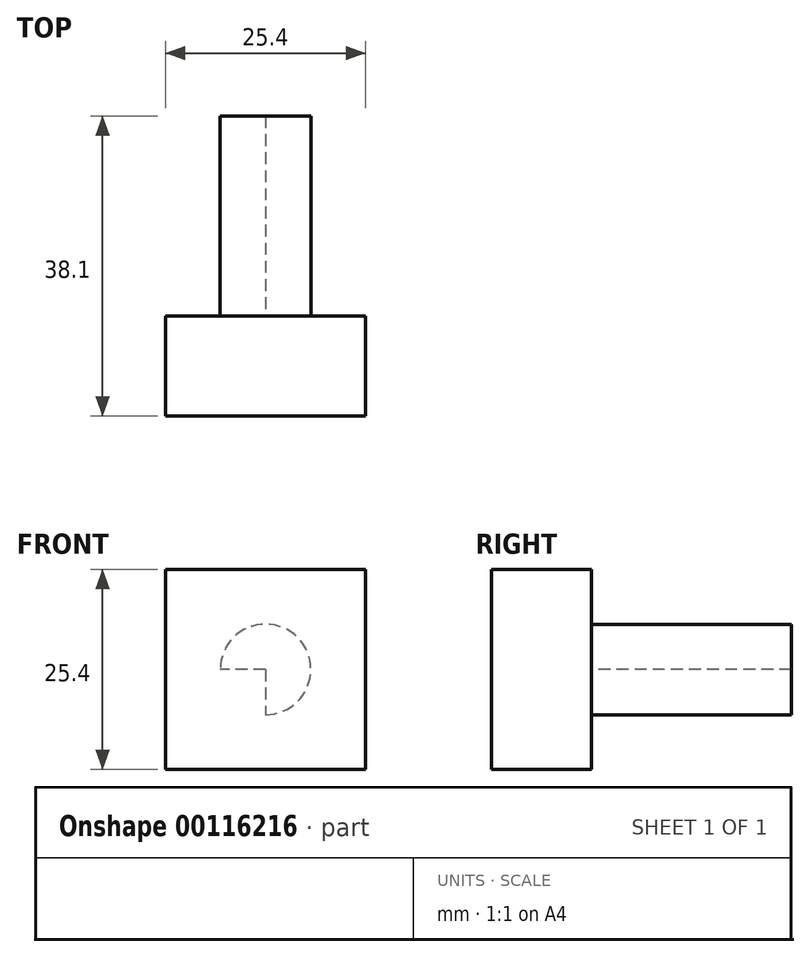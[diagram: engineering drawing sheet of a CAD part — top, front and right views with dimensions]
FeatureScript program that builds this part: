
annotation { "Feature Type Name" : "Feature", "Feature Type Description" : "" }
export const myFeature = defineFeature(function(context is Context, id is Id, definition is map)
    precondition{}
    {
        {
            var Q0;
            Q0=qCreatedBy(makeId("Top.planeOp"),FACE);
            var sketch = newSketch(context, id + "F0", { "sketchPlane" : qUnion([Q0])});
            skLineSegment(sketch, "E0.bottom", {"start": v(0, 12.7) * mm, "end": v(25.4, 12.7) * mm});
            skLineSegment(sketch, "E0.top", {"start": v(0, 0) * mm, "end": v(25.4, 0) * mm});
            skLineSegment(sketch, "E0.left", {"start": v(0, 12.7) * mm, "end": v(0, 0) * mm});
            skLineSegment(sketch, "E0.right", {"start": v(25.4, 12.7) * mm, "end": v(25.4, 0) * mm});
            skSolve(sketch);
        }
        {
            var Q0;
            Q0 = qSketchRegion(id + "F0", true);
            var Q1;
            Q1=makeQuery(id+"F0.imprint","IMPRINT",FACE,{"disambiguationData":[TD([[makeQuery(id+"F0.imprint","IMPRINT",EDGE,{"derivedFrom":sQuery(id+"F0.wireOp",EDGE,"E0.bottom")}),-1.0]])]});
            extrude(context, id + "F1", {"entities" : qUnion([Q0, Q1]), "depth" : 25.4 * mm});
        }
        {
            var Q0;
            Q0=makeQuery(id+"F1.opExtrude","SWEPT_FACE",FACE,{"disambiguationData":[OSD([sQuery(id+"F0.wireOp",EDGE,"E0.bottom")])]});
            var sketch = newSketch(context, id + "F2", { "sketchPlane" : qUnion([Q0])});
            skCircle(sketch, "E1", {"center": v(-12.7, 12.7) * mm, "radius": 6.25 * mm});
            skCircle(sketch, "E2", {"center": v(-12.7, 12.7) * mm, "radius": 5.75 * mm});
            skLineSegment(sketch, "E3", {"start": v(-12.7, 12.7) * mm, "end": v(0, 12.7) * mm});
            skLineSegment(sketch, "E4", {"start": v(-12.7, 12.7) * mm, "end": v(-12.7, 0) * mm});
            skSolve(sketch);
        }
        {
            var Q0;
            {var subQ0=sQuery(id+"F2.wireOp",EDGE,"E3");var subQ1=sQuery(id+"F2.wireOp",EDGE,"E2");var subQ2=makeQuery(id+"F2.imprint","INTERSECT",VERTEX,{"derivedFrom":[subQ1,subQ0]});Q0=makeQuery(id+"F2.imprint","IMPRINT",FACE,{"disambiguationData":[TD([[makeQuery(id+"F2.imprint","IMPRINT",EDGE,{"disambiguationData":[TD([[subQ2,-1.0]])],"derivedFrom":subQ1}),1.0]])]});}
            extrude(context, id + "F3", {"entities" : qUnion([Q0]), "operationType" : NewBodyOperationType.ADD, "depth" : 25.4 * mm});
        }
    });
